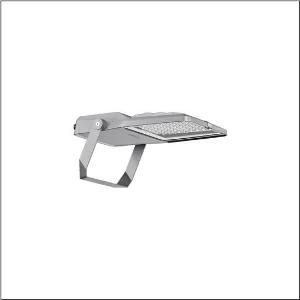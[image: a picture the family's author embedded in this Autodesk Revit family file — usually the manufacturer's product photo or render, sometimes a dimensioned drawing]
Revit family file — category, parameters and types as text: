
# Revit family: floodlight_fl_21_iq_mini___pl64_5xa7772c3e1a_c8ef
name_source: partatom
category: Lighting Fixtures
units: mm (PartAtom-declared; Revit-internal decimal feet)

## family parameters
Cut with Voids When Loaded = No
Host = Face
Light Source = No
Part Type = Normal
Room Calculation Point = No
Round Connector Dimension = Use Diameter
Shared = No

## types (1)
- --- (1 x LED, 10150 lm, 87.2 W, 3000K)
    Apparent Load = 87 VA
    CIE Flux Codes = 28 80 98 100 100
    Color Rendering = 80
    Color Temperature = 3000K
    Default Elevation = 1800 mm
    Description = Floodlight FL 21 iQ mini, floodlight, primary light control with lens, of PMMA, primary optical cover: protective disc, of toughened safety glass, transparent, light distribution: PL64, light emission: direct distribution, installation type: surface-mounted, LED, High Power LED, rated luminous flux: 10.150lm, luminous efficacy: 116lm/W, light colour: 830, colour temperature: 3000K, control: Street-Remote, Auto-Match, Temp-Guard, Night-Set, Smart-Wire, Desk-Remote (wireless, voltage-free reading and setting of iQ features in the workshop via application-optimized NFC function/RFID function), optimised constant luminous flux control (CLO 2.0), with terminal, 6-pole, mains connection: 220..240V, AC, 50/60Hz, start of lifetime: 87W, end of service life: 92W, reduction: 40W, luminaire housing, of diecast aluminium, powder-coated, Siteco® metallic grey (DB 702S), corrosivity category C5 mid according to DIN EN ISO 12944, sealing non-destructively replaceable, mounting bracket, of steel, galvanised, powder-coated, Siteco® metallic grey (DB 702S), protection rating (complete): IP66, insulation class (complete): insulation class II (safety insulation), certification: CE, ENEC, VDE, protection symbol: D, impact resistance: IK08, permissible operating ambient temperature: -40..+40°C, permissible operating ambient temperature for outdoor applications: -40..+50°C, standard: DIN EN 12944, LABS conformity tested according to VDMA 24364:2018-05, packaging unit: 1 piece

Light Distribution: PL64
    Height = 70 mm
    Lamp = 1 x LED
    Lamp Light Flux = 10150 lm
    Lamp Power = 87.2 W
    Lamp count = 1
    Length = 485 mm
    Luminous efficacy = 116 lm/W
    Manufacturer = Siteco
    ModVariant = No
    Model = 5XA7772C3E1A
    Number of Poles = 1
    OnlyDefault = Yes
    Power Factor = 1
    Product Name = Floodlight FL 21 iQ mini | PL64
    Product group = floodlight | pylon annexe
    ProductGroupID = 6200
    Protection Class = Protection class II
    Protection Degree = IP 66
    RLX_Detail_Level = 1
    RLX_Emergency_Light_Flux = 0 lm
    RLX_Emergency_Type = 0
    RLX_Emergency_Type_DB = No
    RlxData = <blob elided: 96209 chars, md5=baf99fba>
    Socket = socket
    Standby Power = 0 W
    System Light Flux = 10150 lm
    System Power = 87 W
    Type Comments = factory setting: luminous flux: 100 % | dim-lin: 254 | 456 mA
    Type Image = l_1006845.jpg
    URL = http://relux.com
    VarID = @adj_098625
    Voltage = 0 V
    Weight = 0.00 kg
    Width = 337 mm

## geometry (parser evidence)
native form markers: Blend x4, Sweep x12
no freeform markers — native parametric forms only
